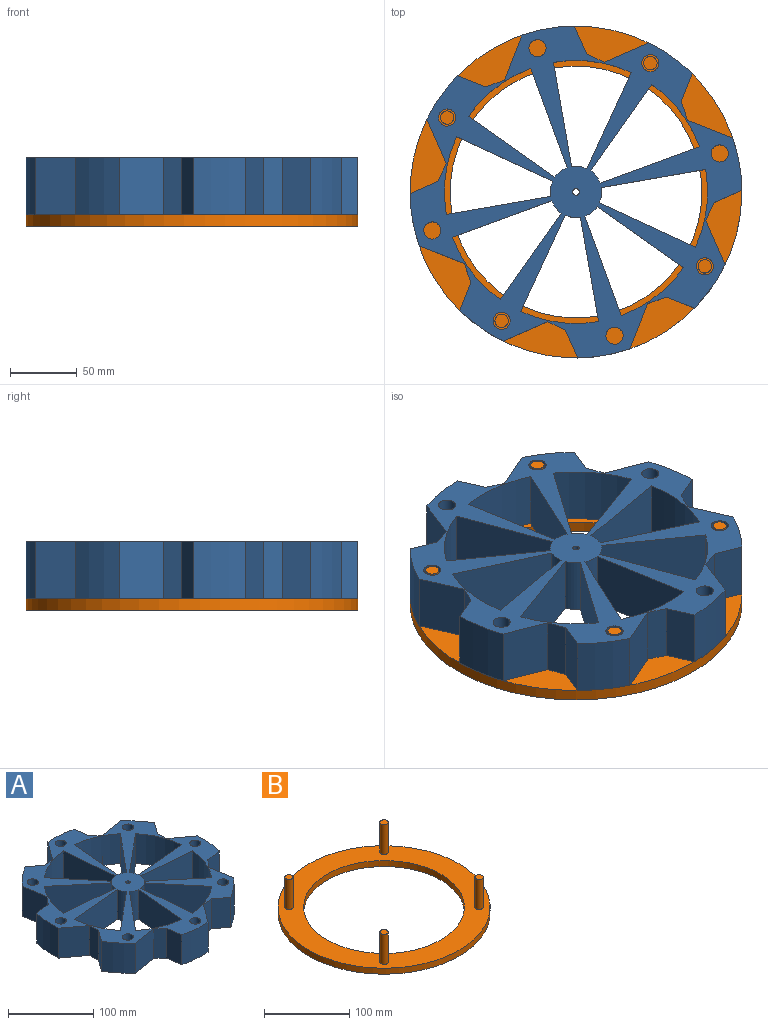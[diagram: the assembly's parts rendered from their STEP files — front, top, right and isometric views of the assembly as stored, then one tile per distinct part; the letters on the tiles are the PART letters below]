
ASSEMBLY  parts=2 mates=1
PART A: 75 faces, bbox 249.4x249.4x43 mm
  f0: plane 43x36.16mm, normal (0.99,0.15,0), area 1572.2mm2, adj f1,f62,f73,f74
  f1: plane 43x11.25mm, normal (0.76,-0.65,0), area 636.1mm2, adj f0,f2,f73,f74
  f2: plane 43x22.51mm, normal (0.15,-0.99,0), area 978.8mm2, adj f1,f3,f73,f74
  f3: cylinder r=124.7mm len=43mm, axis (0,0,-1), area 1722.1mm2, adj f2,f4,f73,f74
  f4: plane 43x29.4mm, normal (0.59,0.8,0), area 1572.2mm2, adj f3,f5,f73,f74
  f5: plane 43x14.75mm, normal (1,0.08,0), area 636.1mm2, adj f4,f6,f73,f74
  f6: plane 43x18.3mm, normal (0.8,-0.59,0), area 978.8mm2, adj f5,f7,f73,f74
  f7: cylinder r=124.7mm len=43mm, axis (0,0,-1), area 1722.1mm2, adj f6,f8,f73,f74
  f8: plane 43x36.16mm, normal (-0.15,0.99,0), area 1572.2mm2, adj f7,f9,f73,f74
  f9: plane 43x11.25mm, normal (0.65,0.76,0), area 636.1mm2, adj f8,f10,f73,f74
  f10: plane 43x22.51mm, normal (0.99,0.15,0), area 978.8mm2, adj f9,f11,f73,f74
  f11: cylinder r=124.7mm len=43mm, axis (0,0,-1), area 1722.1mm2, adj f10,f12,f73,f74
  f12: plane 43x29.4mm, normal (-0.8,0.59,0), area 1572.2mm2, adj f11,f13,f73,f74
  f13: plane 43x14.75mm, normal (-0.08,1,0), area 636.1mm2, adj f12,f14,f73,f74
  f14: plane 43x18.3mm, normal (0.59,0.8,0), area 978.8mm2, adj f13,f15,f73,f74
  f15: cylinder r=124.7mm len=43mm, axis (0,0,-1), area 1722.1mm2, adj f14,f16,f73,f74
  f16: plane 43x36.16mm, normal (-0.99,-0.15,0), area 1572.2mm2, adj f15,f17,f73,f74
  f17: plane 43x11.25mm, normal (-0.76,0.65,0), area 636.1mm2, adj f16,f18,f73,f74
  f18: plane 43x22.51mm, normal (-0.15,0.99,0), area 978.8mm2, adj f17,f19,f73,f74
  f19: cylinder r=124.7mm len=43mm, axis (0,0,-1), area 1722.1mm2, adj f18,f20,f73,f74
  f20: plane 43x29.4mm, normal (-0.59,-0.8,0), area 1572.2mm2, adj f19,f21,f73,f74
  f21: plane 43x14.75mm, normal (-1,-0.08,0), area 636.1mm2, adj f20,f22,f73,f74
  f22: plane 43x18.3mm, normal (-0.8,0.59,0), area 978.8mm2, adj f21,f23,f73,f74
  f23: cylinder r=124.7mm len=43mm, axis (0,0,-1), area 1722.1mm2, adj f22,f24,f73,f74
  f24: plane 43x36.16mm, normal (0.15,-0.99,0), area 1572.2mm2, adj f23,f25,f73,f74
  f25: plane 43x11.25mm, normal (-0.65,-0.76,0), area 636.1mm2, adj f24,f26,f73,f74
  f26: plane 43x22.51mm, normal (-0.99,-0.15,0), area 978.8mm2, adj f25,f27,f73,f74
  f27: cylinder r=124.7mm len=43mm, axis (0,0,-1), area 1722.1mm2, adj f26,f28,f73,f74
  f28: plane 43x29.4mm, normal (0.8,-0.59,0), area 1572.2mm2, adj f27,f29,f73,f74
  f29: plane 43x14.75mm, normal (0.08,-1,0), area 636.1mm2, adj f28,f30,f73,f74
  f30: plane 43x18.3mm, normal (-0.59,-0.8,0), area 978.8mm2, adj f29,f62,f73,f74
  f31: cylinder r=19.35mm len=43mm, axis (0,0,-1), area 504.5mm2, adj f32,f63,f73,f74
  f32: plane 61.06x50.99mm, normal (-0.64,0.77,0), area 3420.7mm2, adj f31,f33,f73,f74
  f33: cylinder r=98.9mm len=54.55mm, axis (0,0,-1), area 2578.3mm2, adj f32,f63,f73,f74
  f34: cylinder r=19.35mm len=43mm, axis (0,0,-1), area 504.5mm2, adj f35,f64,f73,f74
  f35: plane 79.23x43mm, normal (-1,0.09,0), area 3420.7mm2, adj f34,f36,f73,f74
  f36: cylinder r=98.9mm len=54.55mm, axis (0,0,-1), area 2578.3mm2, adj f35,f64,f73,f74
  f37: cylinder r=19.35mm len=43mm, axis (0,0,-1), area 504.5mm2, adj f38,f65,f73,f74
  f38: plane 61.06x50.99mm, normal (-0.77,-0.64,0), area 3420.7mm2, adj f37,f39,f73,f74
  f39: cylinder r=98.9mm len=54.55mm, axis (0,0,-1), area 2578.3mm2, adj f38,f65,f73,f74
  f40: plane 79.23x43mm, normal (-0.09,1,0), area 3420.7mm2, adj f41,f66,f73,f74
  f41: cylinder r=19.35mm len=43mm, axis (0,0,-1), area 504.5mm2, adj f40,f42,f73,f74
  f42: plane 61.06x50.99mm, normal (0.64,-0.77,0), area 3420.6mm2, adj f41,f66,f73,f74
  f43: cylinder r=19.35mm len=43mm, axis (0,0,-1), area 504.5mm2, adj f44,f67,f73,f74
  f44: plane 79.23x43mm, normal (-0.09,-1,0), area 3420.6mm2, adj f43,f45,f73,f74
  f45: cylinder r=98.9mm len=54.55mm, axis (0,0,-1), area 2578.3mm2, adj f44,f67,f73,f74
  f46: cylinder r=19.35mm len=43mm, axis (0,0,-1), area 504.5mm2, adj f47,f68,f73,f74
  f47: plane 79.23x43mm, normal (1,-0.09,0), area 3420.7mm2, adj f46,f48,f73,f74
  f48: cylinder r=98.9mm len=54.55mm, axis (0,0,-1), area 2578.3mm2, adj f47,f68,f73,f74
  f49: plane 61.05x51mm, normal (-0.64,-0.77,0), area 3420.7mm2, adj f50,f70,f73,f74
  f50: cylinder r=19.35mm len=43mm, axis (0,0,-1), area 504.5mm2, adj f49,f51,f73,f74
  f51: plane 79.23x43mm, normal (0.09,1,0), area 3420.6mm2, adj f50,f70,f73,f74
  f52: cylinder r=19.35mm len=43mm, axis (0,0,-1), area 504.5mm2, adj f53,f71,f73,f74
  f53: plane 61.06x50.99mm, normal (0.77,0.64,0), area 3420.7mm2, adj f52,f54,f73,f74
  f54: cylinder r=98.9mm len=54.55mm, axis (0,0,-1), area 2578.3mm2, adj f53,f71,f73,f74
  f55: cylinder r=6.45mm len=43mm, axis (0,0,-1), area 1742.6mm2, adj f73,f74
  f56: cylinder r=6.45mm len=43mm, axis (0,0,-1), area 1742.6mm2, adj f73,f74
  f57: cylinder r=6.45mm len=43mm, axis (0,0,-1), area 1742.6mm2, adj f73,f74
  f58: cylinder r=6.45mm len=43mm, axis (0,0,-1), area 1742.6mm2, adj f73,f74
  f59: cylinder r=6.45mm len=43mm, axis (0,0,-1), area 1742.6mm2, adj f73,f74
  f60: cylinder r=6.45mm len=43mm, axis (0,0,-1), area 1742.6mm2, adj f73,f74
  f61: cylinder r=6.45mm len=43mm, axis (0,0,-1), area 1742.6mm2, adj f73,f74
  f62: cylinder r=124.7mm len=43mm, axis (0,0,-1), area 1722.1mm2, adj f0,f30,f73,f74
  f63: plane 79.23x43mm, normal (0.09,-1,0), area 3420.7mm2, adj f31,f33,f73,f74
  f64: plane 61.05x51mm, normal (0.77,-0.64,0), area 3420.7mm2, adj f34,f36,f73,f74
  f65: plane 79.23x43mm, normal (1,0.09,0), area 3420.7mm2, adj f37,f39,f73,f74
  f66: cylinder r=98.9mm len=54.55mm, axis (0,0,-1), area 2578.3mm2, adj f40,f42,f73,f74
  f67: plane 61.05x51mm, normal (0.64,0.77,0), area 3420.6mm2, adj f43,f45,f73,f74
  f68: plane 61.05x51mm, normal (-0.77,0.64,0), area 3420.6mm2, adj f46,f48,f73,f74
  f69: cylinder r=2.5mm len=43mm, axis (0,0,-1), area 675.4mm2, adj f73,f74
  f70: cylinder r=98.9mm len=54.55mm, axis (0,0,-1), area 2578.3mm2, adj f49,f51,f73,f74
  f71: plane 79.23x43mm, normal (-1,-0.09,0), area 3420.7mm2, adj f52,f54,f73,f74
  f72: cylinder r=6.45mm len=43mm, axis (0,0,-1), area 1742.6mm2, adj f73,f74
  f73: plane 249.4x249.4mm, normal (0,0,1), area 18102.8mm2, adj f0,f1,f2,f3,f4,f5,f6,f7
  f74: plane 249.4x249.4mm, normal (0,0,-1), area 18102.8mm2, adj f0,f1,f2,f3,f4,f5,f6,f7
PART B: 12 faces, bbox 249.4x249.4x51.6 mm
  f0: cylinder r=94.6mm len=189.2mm, axis (0,0,-1), area 5111.7mm2, adj f2,f3
  f1: cylinder r=124.7mm len=249.4mm, axis (0,0,-1), area 6738.2mm2, adj f2,f3
  f2: plane 249.4x249.4mm, normal (0,0,1), area 20423.3mm2, adj f0,f1,f4,f6,f8,f10
  f3: plane 249.4x249.4mm, normal (0,0,-1), area 20737.4mm2, adj f0,f1
  f4: cylinder r=5mm len=43mm, axis (0,0,-1), area 1350.9mm2, adj f2,f5
  f5: plane 10x10mm, normal (0,0,1), area 78.5mm2, adj f4
  f6: cylinder r=5mm len=43mm, axis (0,0,-1), area 1350.9mm2, adj f2,f7
  f7: plane 10x10mm, normal (0,0,1), area 78.5mm2, adj f6
  f8: cylinder r=5mm len=43mm, axis (0,0,-1), area 1350.9mm2, adj f2,f9
  f9: plane 10x10mm, normal (0,0,1), area 78.5mm2, adj f8
  f10: cylinder r=5mm len=43mm, axis (0,0,-1), area 1350.9mm2, adj f2,f11
  f11: plane 10x10mm, normal (0,0,1), area 78.5mm2, adj f10
PLACE A rot(axis=(0,0,1),105deg) t=(-32.11,62.2,-70.14)mm
PLACE B rot(axis=(0,0,1),105deg) t=(-153.5,461.26,-73.14)mm
MATE fastened B.f4 <-> A.f72  axis (0,0,1) through (-127.12,120.68,-20.14)mm
